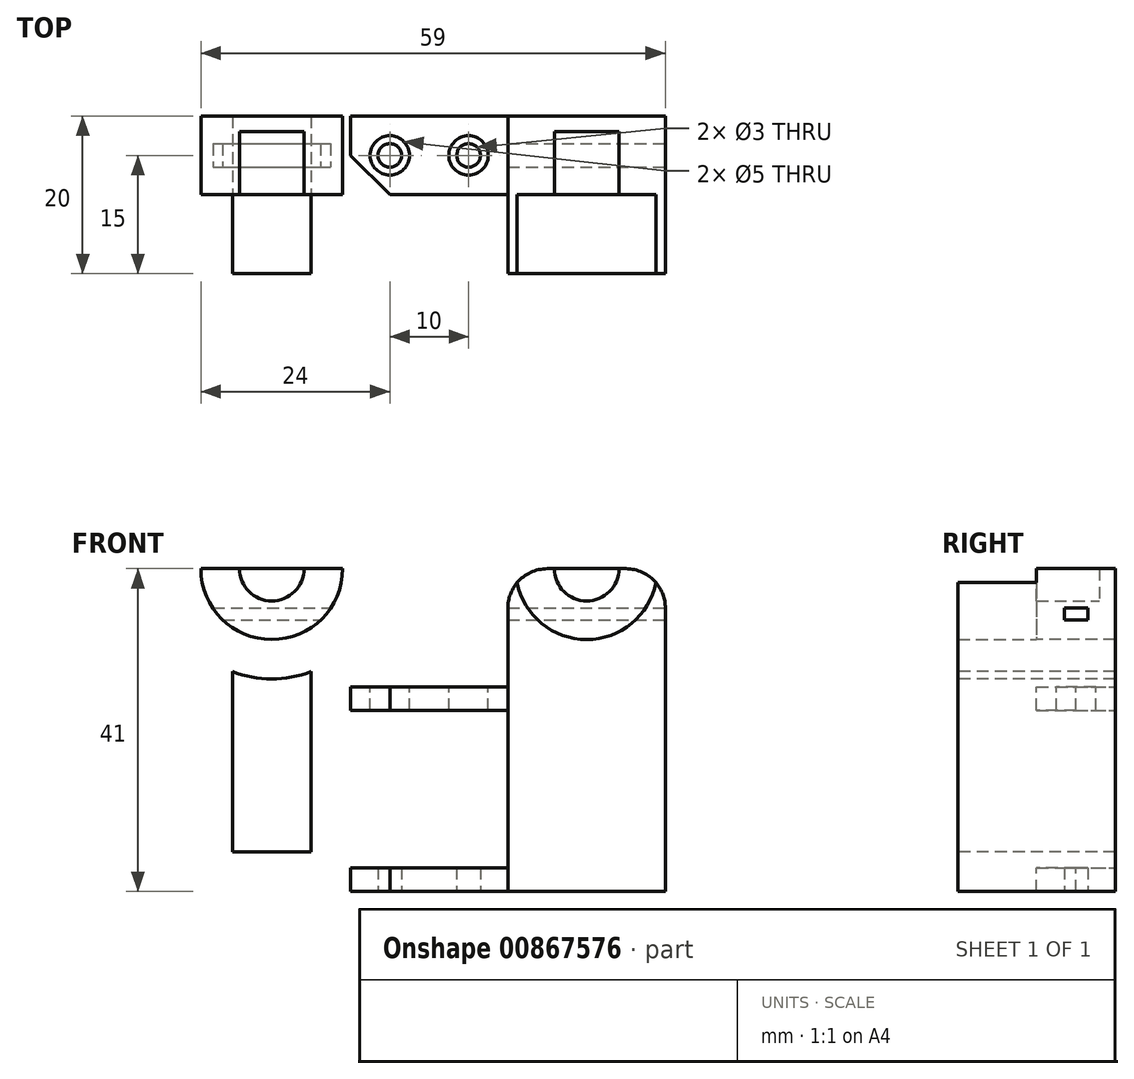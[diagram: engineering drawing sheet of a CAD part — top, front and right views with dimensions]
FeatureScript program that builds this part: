
annotation { "Feature Type Name" : "Feature", "Feature Type Description" : "" }
export const myFeature = defineFeature(function(context is Context, id is Id, definition is map)
    precondition{}
    {
        {
            var Q0;
            Q0=qCreatedBy(makeId("Front.planeOp"),FACE);
            var sketch = newSketch(context, id + "F0", { "sketchPlane" : qUnion([Q0])});
            skArc(sketch, "E0", {"start": v(-4.1, 0) * mm, "mid": v(0, -4.1) * mm, "end": v(4.1, 0) * mm});
            skArc(sketch, "E1", {"start": v(-7, 0) * mm, "mid": v(0, -7) * mm, "end": v(7, 0) * mm});
            skLineSegment(sketch, "E2", {"start": v(7, 0) * mm, "end": v(4.1, 0) * mm});
            skLineSegment(sketch, "E3", {"start": v(-4.1, 0) * mm, "end": v(-7, 0) * mm});
            skLineSegment(sketch, "E4", {"start": v(7, 0) * mm, "end": v(10, 0) * mm});
            skLineSegment(sketch, "E5", {"start": v(-7, 0) * mm, "end": v(-10, 0) * mm});
            skLineSegment(sketch, "E6", {"start": v(-10, 0) * mm, "end": v(-10, -41) * mm});
            skLineSegment(sketch, "E7", {"start": v(-10, -41) * mm, "end": v(10, -41) * mm});
            skLineSegment(sketch, "E8", {"start": v(10, -41) * mm, "end": v(10, 0) * mm});
            skPoint(sketch, "E9", {"position": v(20, 0) * mm});
            skLineSegment(sketch, "E10", {"start": v(20, 0) * mm, "end": v(20, -41) * mm});
            skLineSegment(sketch, "E11.MirrorCS", {"start": v(47, 0) * mm, "end": v(50, 0) * mm});
            skLineSegment(sketch, "E12.MirrorCS", {"start": v(44.1, 0) * mm, "end": v(47, 0) * mm});
            skLineSegment(sketch, "E13.MirrorCS", {"start": v(50, -41) * mm, "end": v(30, -41) * mm});
            skLineSegment(sketch, "E14.MirrorCS", {"start": v(33, 0) * mm, "end": v(30, 0) * mm});
            skLineSegment(sketch, "E15.MirrorCS", {"start": v(50, 0) * mm, "end": v(50, -41) * mm});
            skArc(sketch, "E16.MirrorCS", {"start": v(47, 0) * mm, "mid": v(40, -7) * mm, "end": v(33, 0) * mm});
            skLineSegment(sketch, "E17.MirrorCS", {"start": v(33, 0) * mm, "end": v(35.9, 0) * mm});
            skLineSegment(sketch, "E18.MirrorCS", {"start": v(30, -41) * mm, "end": v(30, 0) * mm});
            skArc(sketch, "E19.MirrorCS", {"start": v(44.1, 0) * mm, "mid": v(40, -4.1) * mm, "end": v(35.9, 0) * mm});
            skSolve(sketch);
        }
        {
            var Q0;
            Q0=makeQuery(id+"F0.imprint","IMPRINT",FACE,{"disambiguationData":[TD([[makeQuery(id+"F0.imprint","IMPRINT",EDGE,{"derivedFrom":sQuery(id+"F0.wireOp",EDGE,"E1")}),-1.0]])]});
            var Q1;
            Q1=makeQuery(id+"F0.imprint","IMPRINT",FACE,{"disambiguationData":[TD([[makeQuery(id+"F0.imprint","IMPRINT",EDGE,{"derivedFrom":sQuery(id+"F0.wireOp",EDGE,"E0")}),-1.0]])]});
            var Q2;
            Q2=makeQuery(id+"F0.imprint","IMPRINT",FACE,{"disambiguationData":[TD([[makeQuery(id+"F0.imprint","IMPRINT",EDGE,{"derivedFrom":sQuery(id+"F0.wireOp",EDGE,"E11.MirrorCS")}),-1.0]])]});
            var Q3;
            Q3=makeQuery(id+"F0.imprint","IMPRINT",FACE,{"disambiguationData":[TD([[makeQuery(id+"F0.imprint","IMPRINT",EDGE,{"derivedFrom":sQuery(id+"F0.wireOp",EDGE,"E12.MirrorCS")}),-1.0]])]});
            extrude(context, id + "F1", {"entities" : qUnion([Q0, Q1, Q2, Q3]), "depth" : 10 * mm, "offsetDistance" : 25 * mm});
        }
        {
            var Q0;
            Q0=makeQuery(id+"F1.opExtrude","SWEPT_FACE",FACE,{"disambiguationData":[OSD([sQuery(id+"F0.wireOp",EDGE,"E3"),sQuery(id+"F0.wireOp",EDGE,"E5")])]});
            var sketch = newSketch(context, id + "F2", { "sketchPlane" : qUnion([Q0])});
            skLineSegment(sketch, "E20.bottom", {"start": v(-10, 0) * mm, "end": v(10, 0) * mm});
            skLineSegment(sketch, "E20.top", {"start": v(-10, -2) * mm, "end": v(10, -2) * mm});
            skLineSegment(sketch, "E20.left", {"start": v(-10, 0) * mm, "end": v(-10, -2) * mm});
            skLineSegment(sketch, "E20.right", {"start": v(10, 0) * mm, "end": v(10, -2) * mm});
            skPoint(sketch, "E21", {"position": v(20, 0) * mm});
            skLineSegment(sketch, "E22.MirrorCS", {"start": v(-10, 0) * mm, "end": v(-10, 2) * mm});
            skLineSegment(sketch, "E23.MirrorCS", {"start": v(10, 0) * mm, "end": v(10, 2) * mm});
            skLineSegment(sketch, "E24.MirrorCS", {"start": v(-10, 2) * mm, "end": v(10, 2) * mm});
            skLineSegment(sketch, "E25", {"start": v(20, 0) * mm, "end": v(20, -10.23) * mm});
            skLineSegment(sketch, "E26.MirrorCS", {"start": v(50, 0) * mm, "end": v(50, 2) * mm});
            skLineSegment(sketch, "E27.MirrorCS", {"start": v(30, 0) * mm, "end": v(30, -2) * mm});
            skLineSegment(sketch, "E28.MirrorCS", {"start": v(30, 0) * mm, "end": v(30, 2) * mm});
            skLineSegment(sketch, "E29.MirrorCS", {"start": v(50, 0) * mm, "end": v(50, -2) * mm});
            skLineSegment(sketch, "E30.MirrorCS", {"start": v(50, 0) * mm, "end": v(30, 0) * mm});
            skLineSegment(sketch, "E31.MirrorCS", {"start": v(50, 2) * mm, "end": v(30, 2) * mm});
            skLineSegment(sketch, "E32.MirrorCS", {"start": v(50, -2) * mm, "end": v(30, -2) * mm});
            skSolve(sketch);
        }
        {
            var Q0;
            {var subQ3=sQuery(id+"F2.wireOp",EDGE,"E20.right");Q0=makeQuery(id+"F2.imprint","IMPRINT",FACE,{"disambiguationData":[TD([[makeQuery(id+"F2.imprint","IMPRINT",EDGE,{"derivedFrom":subQ3}),-1.0]])]});}
            var Q1;
            Q1=makeQuery(id+"F2.imprint","IMPRINT",FACE,{"disambiguationData":[TD([[makeQuery(id+"F2.imprint","IMPRINT",EDGE,{"derivedFrom":sQuery(id+"F2.wireOp",EDGE,"E27.MirrorCS")}),1.0]])]});
            extrude(context, id + "F3", {"entities" : qUnion([Q0, Q1]), "operationType" : NewBodyOperationType.ADD, "oppositeDirection" : true, "depth" : 10 * mm, "offsetDistance" : 25 * mm});
        }
        {
            var Q0;
            Q0=makeQuery(id+"F1.opExtrude","CAP_FACE",FACE,{"disambiguationData":[OSD([sQuery(id+"F0.wireOp",EDGE,"E0"),sQuery(id+"F0.wireOp",EDGE,"E2"),sQuery(id+"F0.wireOp",EDGE,"E3"),sQuery(id+"F0.wireOp",EDGE,"E4"),sQuery(id+"F0.wireOp",EDGE,"E5"),sQuery(id+"F0.wireOp",EDGE,"E6"),sQuery(id+"F0.wireOp",EDGE,"E7"),sQuery(id+"F0.wireOp",EDGE,"E8")])],"isStart":false});
            var sketch = newSketch(context, id + "F4", { "sketchPlane" : qUnion([Q0])});
            skCircle(sketch, "E33", {"center": v(0, 0) * mm, "radius": 9 * mm});
            skLineSegment(sketch, "E34", {"start": v(-9, 0) * mm, "end": v(-10, 0) * mm});
            skLineSegment(sketch, "E35", {"start": v(-10, 0) * mm, "end": v(-10, -41) * mm});
            skLineSegment(sketch, "E36", {"start": v(-10, -41) * mm, "end": v(10, -41) * mm});
            skLineSegment(sketch, "E37", {"start": v(10, -41) * mm, "end": v(10, 0) * mm});
            skLineSegment(sketch, "E38", {"start": v(10, 0) * mm, "end": v(9, 0) * mm});
            skLineSegment(sketch, "E39", {"start": v(20, 0) * mm, "end": v(20, -22.34) * mm});
            skLineSegment(sketch, "E40.MirrorCS", {"start": v(30, 0) * mm, "end": v(31, 0) * mm});
            skLineSegment(sketch, "E41.MirrorCS", {"start": v(49, 0) * mm, "end": v(50, 0) * mm});
            skCircle(sketch, "E42.MirrorC", {"center": v(40, 0) * mm, "radius": 9 * mm});
            skLineSegment(sketch, "E43.MirrorCS", {"start": v(30, -41) * mm, "end": v(30, 0) * mm});
            skLineSegment(sketch, "E44.MirrorCS", {"start": v(50, 0) * mm, "end": v(50, -41) * mm});
            skLineSegment(sketch, "E45.MirrorCS", {"start": v(50, -41) * mm, "end": v(30, -41) * mm});
            skSolve(sketch);
        }
        {
            var Q0;
            {var subQ0=sQuery(id+"F4.wireOp",EDGE,"E34");Q0=makeQuery(id+"F4.imprint","IMPRINT",FACE,{"disambiguationData":[TD([[makeQuery(id+"F4.imprint","IMPRINT",EDGE,{"derivedFrom":subQ0}),1.0]])]});}
            var Q1;
            {var subQ1=sQuery(id+"F4.wireOp",EDGE,"E40.MirrorCS");Q1=makeQuery(id+"F4.imprint","IMPRINT",FACE,{"disambiguationData":[TD([[makeQuery(id+"F4.imprint","IMPRINT",EDGE,{"derivedFrom":subQ1}),-1.0]])]});}
            extrude(context, id + "F5", {"entities" : qUnion([Q0, Q1]), "operationType" : NewBodyOperationType.ADD, "depth" : 10 * mm, "offsetDistance" : 25 * mm});
        }
        {
            var Q0;
            Q0=makeQuery(id+"F5.opExtrude","CAP_FACE",FACE,{"disambiguationData":[OSD([sQuery(id+"F4.wireOp",EDGE,"E33"),sQuery(id+"F4.wireOp",EDGE,"E34"),sQuery(id+"F4.wireOp",EDGE,"E35"),sQuery(id+"F4.wireOp",EDGE,"E36"),sQuery(id+"F4.wireOp",EDGE,"E37"),sQuery(id+"F4.wireOp",EDGE,"E38")])],"isStart":false});
            var sketch = newSketch(context, id + "F6", { "sketchPlane" : qUnion([Q0])});
            skArc(sketch, "E46.0", {"start": v(45, -13.08) * mm, "mid": v(40, -14) * mm, "end": v(35, -13.08) * mm});
            skLineSegment(sketch, "E46.1", {"start": v(45, -36) * mm, "end": v(45, -13.08) * mm});
            skLineSegment(sketch, "E46.2", {"start": v(35, -36) * mm, "end": v(45, -36) * mm});
            skLineSegment(sketch, "E46.3", {"start": v(35, -13.08) * mm, "end": v(35, -36) * mm});
            skArc(sketch, "E47.0", {"start": v(5, -13.08) * mm, "mid": v(0, -14) * mm, "end": v(-5, -13.08) * mm});
            skLineSegment(sketch, "E47.1", {"start": v(5, -36) * mm, "end": v(5, -13.08) * mm});
            skLineSegment(sketch, "E47.2", {"start": v(-5, -36) * mm, "end": v(5, -36) * mm});
            skLineSegment(sketch, "E47.3", {"start": v(-5, -13.08) * mm, "end": v(-5, -36) * mm});
            skSolve(sketch);
        }
        {
            var Q0;
            Q0=makeQuery(id+"F6.imprint","IMPRINT",FACE,{"disambiguationData":[TD([[makeQuery(id+"F6.imprint","IMPRINT",EDGE,{"derivedFrom":sQuery(id+"F6.wireOp",EDGE,"E47.0")}),1.0]])]});
            var Q1;
            Q1=makeQuery(id+"F6.imprint","IMPRINT",FACE,{"disambiguationData":[TD([[makeQuery(id+"F6.imprint","IMPRINT",EDGE,{"derivedFrom":sQuery(id+"F6.wireOp",EDGE,"E46.0")}),1.0]])]});
            extrude(context, id + "F7", {"entities" : qUnion([Q0, Q1]), "operationType" : NewBodyOperationType.REMOVE, "oppositeDirection" : true, "depth" : 25 * mm, "offsetDistance" : 25 * mm});
        }
        {
            var Q0;
            Q0=makeQuery(id+"F5.boolean.opBoolean","MERGE",FACE,{"derivedFrom":[makeQuery(id+"F1.opExtrude","SWEPT_FACE",FACE,{"disambiguationData":[OSD([sQuery(id+"F0.wireOp",EDGE,"E15.MirrorCS")])]}),makeQuery(id+"F5.opExtrude","SWEPT_FACE",FACE,{"disambiguationData":[OSD([sQuery(id+"F4.wireOp",EDGE,"E44.MirrorCS")])]})]});
            var sketch = newSketch(context, id + "F8", { "sketchPlane" : qUnion([Q0])});
            skLineSegment(sketch, "E48.bottom", {"start": v(-6.5, -5) * mm, "end": v(-3.5, -5) * mm});
            skLineSegment(sketch, "E48.top", {"start": v(-6.5, -6.5) * mm, "end": v(-3.5, -6.5) * mm});
            skLineSegment(sketch, "E48.left", {"start": v(-6.5, -5) * mm, "end": v(-6.5, -6.5) * mm});
            skLineSegment(sketch, "E48.right", {"start": v(-3.5, -5) * mm, "end": v(-3.5, -6.5) * mm});
            skSolve(sketch);
        }
        {
            var Q0;
            Q0=makeQuery(id+"F8.imprint","IMPRINT",FACE,{"disambiguationData":[TD([[makeQuery(id+"F8.imprint","IMPRINT",EDGE,{"derivedFrom":sQuery(id+"F8.wireOp",EDGE,"E48.bottom")}),-1.0]])]});
            extrude(context, id + "F9", {"entities" : qUnion([Q0]), "operationType" : NewBodyOperationType.REMOVE, "oppositeDirection" : true, "depth" : 100 * mm, "offsetDistance" : 25 * mm});
        }
        {
            var Q0;
            Q0=makeQuery(id+"F5.boolean.opBoolean","MERGE",EDGE,{"derivedFrom":[makeQuery(id+"F1.opExtrude","SWEPT_EDGE",EDGE,{"disambiguationData":[OSD([sQuery(id+"F0.wireOp",EDGE,"E14.MirrorCS"),sQuery(id+"F0.wireOp",EDGE,"E18.MirrorCS")])]}),makeQuery(id+"F5.opExtrude","SWEPT_EDGE",EDGE,{"disambiguationData":[OSD([sQuery(id+"F4.wireOp",EDGE,"E40.MirrorCS"),sQuery(id+"F4.wireOp",EDGE,"E43.MirrorCS")])]})]});
            var Q1;
            Q1=makeQuery(id+"F5.boolean.opBoolean","MERGE",EDGE,{"derivedFrom":[makeQuery(id+"F1.opExtrude","SWEPT_EDGE",EDGE,{"disambiguationData":[OSD([sQuery(id+"F0.wireOp",EDGE,"E11.MirrorCS"),sQuery(id+"F0.wireOp",EDGE,"E15.MirrorCS")])]}),makeQuery(id+"F5.opExtrude","SWEPT_EDGE",EDGE,{"disambiguationData":[OSD([sQuery(id+"F4.wireOp",EDGE,"E41.MirrorCS"),sQuery(id+"F4.wireOp",EDGE,"E44.MirrorCS")])]})]});
            var Q2;
            Q2=makeQuery(id+"F5.boolean.opBoolean","MERGE",EDGE,{"derivedFrom":[makeQuery(id+"F1.opExtrude","SWEPT_EDGE",EDGE,{"disambiguationData":[OSD([sQuery(id+"F0.wireOp",EDGE,"E5"),sQuery(id+"F0.wireOp",EDGE,"E6")])]}),makeQuery(id+"F5.opExtrude","SWEPT_EDGE",EDGE,{"disambiguationData":[OSD([sQuery(id+"F4.wireOp",EDGE,"E34"),sQuery(id+"F4.wireOp",EDGE,"E35")])]})]});
            var Q3;
            Q3=makeQuery(id+"F5.boolean.opBoolean","MERGE",EDGE,{"derivedFrom":[makeQuery(id+"F1.opExtrude","SWEPT_EDGE",EDGE,{"disambiguationData":[OSD([sQuery(id+"F0.wireOp",EDGE,"E4"),sQuery(id+"F0.wireOp",EDGE,"E8")])]}),makeQuery(id+"F5.opExtrude","SWEPT_EDGE",EDGE,{"disambiguationData":[OSD([sQuery(id+"F4.wireOp",EDGE,"E37"),sQuery(id+"F4.wireOp",EDGE,"E38")])]})]});
            fillet(context, id + "F10", {"entities" : qUnion([Q0, Q1, Q2, Q3]), "radius" : 5 * mm, "tangentPropagation" : true, "allowEdgeOverflow" : false});
        }
        {
            var Q0;
            Q0=makeQuery(id+"F3.boolean.opBoolean","MERGE",FACE,{"derivedFrom":[makeQuery(id+"F1.opExtrude","CAP_FACE",FACE,{"disambiguationData":[OSD([sQuery(id+"F0.wireOp",EDGE,"E11.MirrorCS"),sQuery(id+"F0.wireOp",EDGE,"E12.MirrorCS"),sQuery(id+"F0.wireOp",EDGE,"E13.MirrorCS"),sQuery(id+"F0.wireOp",EDGE,"E14.MirrorCS"),sQuery(id+"F0.wireOp",EDGE,"E15.MirrorCS"),sQuery(id+"F0.wireOp",EDGE,"E17.MirrorCS"),sQuery(id+"F0.wireOp",EDGE,"E18.MirrorCS"),sQuery(id+"F0.wireOp",EDGE,"E19.MirrorCS")])],"isStart":true}),makeQuery(id+"F3.opExtrude","SWEPT_FACE",FACE,{"disambiguationData":[OSD([sQuery(id+"F2.wireOp",EDGE,"E30.MirrorCS")])]})]});
            var sketch = newSketch(context, id + "F11", { "sketchPlane" : qUnion([Q0])});
            skLineSegment(sketch, "E49.bottom", {"start": v(-30, -41) * mm, "end": v(-10, -41) * mm});
            skLineSegment(sketch, "E49.top", {"start": v(-30, -38) * mm, "end": v(-10, -38) * mm});
            skLineSegment(sketch, "E49.left", {"start": v(-30, -41) * mm, "end": v(-30, -38) * mm});
            skLineSegment(sketch, "E49.right", {"start": v(-10, -41) * mm, "end": v(-10, -38) * mm});
            skLineSegment(sketch, "E50.bottom", {"start": v(-30, -15) * mm, "end": v(-10, -15) * mm});
            skLineSegment(sketch, "E50.top", {"start": v(-30, -18) * mm, "end": v(-10, -18) * mm});
            skLineSegment(sketch, "E50.left", {"start": v(-30, -15) * mm, "end": v(-30, -18) * mm});
            skLineSegment(sketch, "E50.right", {"start": v(-10, -15) * mm, "end": v(-10, -18) * mm});
            skSolve(sketch);
        }
        {
            var Q0;
            Q0=makeQuery(id+"F11.imprint","IMPRINT",FACE,{"disambiguationData":[TD([[makeQuery(id+"F11.imprint","IMPRINT",EDGE,{"derivedFrom":sQuery(id+"F11.wireOp",EDGE,"E49.bottom")}),1.0]])]});
            var Q1;
            Q1=makeQuery(id+"F11.imprint","IMPRINT",FACE,{"disambiguationData":[TD([[makeQuery(id+"F11.imprint","IMPRINT",EDGE,{"derivedFrom":sQuery(id+"F11.wireOp",EDGE,"E50.bottom")}),-1.0]])]});
            extrude(context, id + "F12", {"entities" : qUnion([Q0, Q1]), "operationType" : NewBodyOperationType.ADD, "oppositeDirection" : true, "depth" : 10 * mm, "offsetDistance" : 25 * mm});
        }
        {
            var Q0;
            Q0=makeQuery(id+"F12.boolean.opBoolean","MERGE",FACE,{"derivedFrom":[makeQuery(id+"F5.boolean.opBoolean","MERGE",FACE,{"derivedFrom":[makeQuery(id+"F1.opExtrude","SWEPT_FACE",FACE,{"disambiguationData":[OSD([sQuery(id+"F0.wireOp",EDGE,"E7")])]}),makeQuery(id+"F5.opExtrude","SWEPT_FACE",FACE,{"disambiguationData":[OSD([sQuery(id+"F4.wireOp",EDGE,"E36")])]})]}),makeQuery(id+"F5.boolean.opBoolean","MERGE",FACE,{"derivedFrom":[makeQuery(id+"F1.opExtrude","SWEPT_FACE",FACE,{"disambiguationData":[OSD([sQuery(id+"F0.wireOp",EDGE,"E13.MirrorCS")])]}),makeQuery(id+"F5.opExtrude","SWEPT_FACE",FACE,{"disambiguationData":[OSD([sQuery(id+"F4.wireOp",EDGE,"E45.MirrorCS")])]})]}),makeQuery(id+"F12.opExtrude","SWEPT_FACE",FACE,{"disambiguationData":[OSD([sQuery(id+"F11.wireOp",EDGE,"E49.bottom")])]})]});
            var sketch = newSketch(context, id + "F13", { "sketchPlane" : qUnion([Q0])});
            skPoint(sketch, "E51", {"position": v(15, 5) * mm});
            skPoint(sketch, "E52", {"position": v(25, 5) * mm});
            skCircle(sketch, "E53", {"center": v(15, 5) * mm, "radius": 1.5 * mm});
            skCircle(sketch, "E54", {"center": v(25, 5) * mm, "radius": 1.5 * mm});
            skSolve(sketch);
        }
        {
            var Q0;
            Q0=makeQuery(id+"F13.imprint","IMPRINT",FACE,{"disambiguationData":[TD([[makeQuery(id+"F13.imprint","IMPRINT",EDGE,{"derivedFrom":sQuery(id+"F13.wireOp",EDGE,"E53")}),1.0]])]});
            var Q1;
            Q1=makeQuery(id+"F13.imprint","IMPRINT",FACE,{"disambiguationData":[TD([[makeQuery(id+"F13.imprint","IMPRINT",EDGE,{"derivedFrom":sQuery(id+"F13.wireOp",EDGE,"E54")}),1.0]])]});
            extrude(context, id + "F14", {"entities" : qUnion([Q0, Q1]), "operationType" : NewBodyOperationType.REMOVE, "oppositeDirection" : true, "depth" : 50 * mm, "offsetDistance" : 25 * mm});
        }
        {
            var Q0;
            Q0=makeQuery(id+"F12.opExtrude","SWEPT_FACE",FACE,{"disambiguationData":[OSD([sQuery(id+"F11.wireOp",EDGE,"E50.bottom")])]});
            var sketch = newSketch(context, id + "F15", { "sketchPlane" : qUnion([Q0])});
            skCircle(sketch, "E55", {"center": v(15, -5) * mm, "radius": 2.5 * mm});
            skCircle(sketch, "E56", {"center": v(25, -5) * mm, "radius": 2.5 * mm});
            skSolve(sketch);
        }
        {
            var Q0;
            Q0=makeQuery(id+"F15.imprint","IMPRINT",FACE,{"disambiguationData":[TD([[makeQuery(id+"F15.imprint","IMPRINT",EDGE,{"derivedFrom":sQuery(id+"F15.wireOp",EDGE,"E55")}),1.0]])]});
            var Q1;
            Q1=makeQuery(id+"F15.imprint","IMPRINT",FACE,{"disambiguationData":[TD([[makeQuery(id+"F15.imprint","IMPRINT",EDGE,{"derivedFrom":sQuery(id+"F15.wireOp",EDGE,"E56")}),1.0]])]});
            extrude(context, id + "F16", {"entities" : qUnion([Q0, Q1]), "operationType" : NewBodyOperationType.REMOVE, "oppositeDirection" : true, "depth" : 10 * mm, "offsetDistance" : 25 * mm});
        }
        {
            var Q0;
            Q0=makeQuery(id+"F12.opExtrude","CAP_EDGE",EDGE,{"disambiguationData":[OSD([sQuery(id+"F11.wireOp",EDGE,"E49.left")])],"isStart":false});
            var Q1;
            Q1=makeQuery(id+"F12.opExtrude","CAP_EDGE",EDGE,{"disambiguationData":[OSD([sQuery(id+"F11.wireOp",EDGE,"E49.right")])],"isStart":false});
            var Q2;
            Q2=makeQuery(id+"F12.opExtrude","CAP_EDGE",EDGE,{"disambiguationData":[OSD([sQuery(id+"F11.wireOp",EDGE,"E50.left")])],"isStart":false});
            var Q3;
            Q3=makeQuery(id+"F12.opExtrude","CAP_EDGE",EDGE,{"disambiguationData":[OSD([sQuery(id+"F11.wireOp",EDGE,"E50.right")])],"isStart":false});
            chamfer(context, id + "F17", {"entities" : qUnion([Q0, Q1, Q2, Q3]), "width" : 5 * mm, "tangentPropagation" : true});
        }
    });
